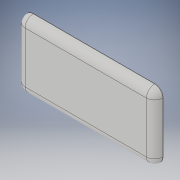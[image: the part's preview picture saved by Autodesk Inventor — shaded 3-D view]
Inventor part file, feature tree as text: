
AUTODESK INVENTOR PART (.ipt)
format: ipt  version: 2019 (Build 230136000, 136)  size: 116,224 bytes
history: native  units: in
note: dims shown in document units (in); Inventor stores cm internally (conversion verified against a paired STEP export)
features: extrude x1, fillet x1, sketch x1
ambient origin geometry x8: Origin, YZ Plane, XZ Plane, XY Plane, X Axis, Y Axis, Z Axis, Center Point
bodies: Solid1 (feature_tree)
feature tree (3):
  extrude  "Extrusion1"  Depth=4.04in
  fillet  "Fillet1"  Radius=0.25in
  sketch  "Sketch1"  dims[d0=1.975in d1=4.04in d2=0.25in d3=0.0in d4=0.24in]
